# Revit family: VIESSMANN - Vitoradial 300-T
name_source: partatom
category: Wyposażenie mechaniczne
revit_build: Autodesk Revit 2017 (Build: 20160720_1515(x64)
units: mm (PartAtom-declared; Revit-internal decimal feet)

## family parameters
Numer OmniClass = 23.15.30.27.21
Oparty na płaszczyźnie roboczej = Nie
Punkt obliczania pomieszczeń = Nie
Tnij formami wycięć po wczytaniu = Tak
Typ części = Normalny
Tytuł OmniClass = Gas Tanks and Gasholders
Współdzielony = Nie
Wymiar okrągłego złącza = Użyj średnicy
Zawsze pionowo = Tak

## types (6) — shared parameters
Autor = https://www.archispace.pl
Dop. ciśnienie robocze = 400000.0 Pa
Dop. temperatura na zasilaniu (=temperatura progowa) = 110 °C
Numer identyfikacyjny produktu = CE-0035BU104
Opis = Olejowo-gazowy kocioł grzewczy
Opis indeksowy = CE-0035BU104
Parametry spalin - dyspozycyjne ciśnienie tłoczenia na króćcu spalin = 70.0 Pa
Parametry spalin - przepływ masowy przy zastosowaniu lekkiego oleju opałowego = 1.5 x moc spalania w kW
Parametry spalin - przepływ masowy spalin w przypadku gazu ziemnego = 1.5225 x moc spalania w kW
Producent = Viessmann Sp.z.o.o.
Przyłącze spalin = 200 mm  [stored 0.656168 ft]
Sprawność znormalizowana (do eksploatacji na olej opałowy) przy temp. systemu grzewczego 75/60°C = 97 (Hs)/103 (Hi) [%]
Spust = 1 1/4"
URL = https://www.viessmann-projektant.pl
Viessmann Kolor 1 = Viessmann Kolor 1
Viessmann Kolor 2 = Viessmann Kolor 2
Viessmann Kolor 3 = Viessmann Kolor 3
Viessmann Kolor 4 = Viessmann Kolor 4
Wysokość fundamentu = 100 mm  [stored 0.328084 ft]
Występ króćca spalin bez WT = 175 mm  [stored 0.574147 ft]
r+62 = 237 mm  [stored 0.777559 ft]

## per-type parameters (varying)
- VR3 101kW: (t-q)+o=195 mm  [stored 0.639764 ft]; Długość=1300 mm; Długość WT=440 mm  [stored 1.44357 ft]; Długość fundamentu=1000 mm  [stored 3.28084 ft]; Masa całkowita=510.00 kg; Masa korpusu kotła=370.00 kg; Moc nominalna=101000 W; Model=Olejowo-gazowy kocioł kondensacyjny Viessmann Vitoradial 300-T VR3 101kW / Oil-gas condensing boiler Viessmann Vitoradial 300-T VR3 101kW; Odsunięcie króćca zasilania z kotła=165 mm; Odsunięcie powrotu do kotła=620 mm  [stored 2.03412 ft]; Odsunięcie przyłącza zabezpieczającego=320 mm  [stored 1.04987 ft]; Odsunięcie strefy serwisowej z przodu=800 mm  [stored 2.62467 ft]; Opory przepływu=220.0 Pa; Opór przepływu spalin=55.0 Pa; PN 6 DN - powrót do kotła=65 mm  [stored 0.213255 ft]; PN 6 DN - zasilanie z kotła=65 mm  [stored 0.213255 ft]; Parametry spalin - przy obciążeniu częściowym (przy temp. wody na powrocie wyn. 30°C)=30 °C; Parametry spalin - przy znamionowej mocy cieplnej (przy temp. wody na powrocie wyn. 30°C)=35 °C; Parametry spalin - temperatura (przy temp. wody na powrocie wyn. 60°C)=60 °C; Pojemność wodna kotła=185.0 L; Promień a=68 mm; Promień b=85 mm  [stored 0.278871 ft]; Przepływ maksymalny=1.2 L/s; Przyłącze zabezpieczające (zawór bezpieczeństwa)=1 1/4"; Straty energii dyżurnej qB,70=1.5 %; Szerokość=755 mm  [stored 2.47703 ft]; Szerokość fundamentu=760 mm; Szerokość podestu=575 mm  [stored 1.88648 ft]; Wysokośc powrotu do kotła=1370 mm; Wysokośc przyłącza splain bez WT=1460 mm; Wysokość=1085 mm; Wysokość d=440 mm  [stored 1.44357 ft]; Wysokość e=650 mm  [stored 2.13255 ft]; Wysokość konsoli=1315 mm; Wysokość króćća zasilania z kotła=1145 mm; Wysokość spustu=200 mm  [stored 0.656168 ft]; Znamionowe obciążenie cieplne=97000 W; Średnica a=135 mm  [stored 0.442913 ft]
- VR3 129kW: (t-q)+o=190 mm  [stored 0.62336 ft]; Długość=1500 mm; Długość WT=440 mm  [stored 1.44357 ft]; Długość fundamentu=1200 mm; Masa całkowita=545.00 kg; Masa korpusu kotła=405.00 kg; Moc nominalna=129000 W; Model=Olejowo-gazowy kocioł kondensacyjny Viessmann Vitoradial 300-T VR3 129kW / Oil-gas condensing boiler Viessmann Vitoradial 300-T VR3 129kW; Odsunięcie króćca zasilania z kotła=165 mm; Odsunięcie powrotu do kotła=825 mm  [stored 2.70669 ft]; Odsunięcie przyłącza zabezpieczającego=395 mm  [stored 1.29593 ft]; Odsunięcie strefy serwisowej z przodu=950 mm  [stored 3.1168 ft]; Opory przepływu=350.0 Pa; Opór przepływu spalin=80.0 Pa; PN 6 DN - powrót do kotła=65 mm  [stored 0.213255 ft]; PN 6 DN - zasilanie z kotła=65 mm  [stored 0.213255 ft]; Parametry spalin - przy obciążeniu częściowym (przy temp. wody na powrocie wyn. 30°C)=35 °C; Parametry spalin - przy znamionowej mocy cieplnej (przy temp. wody na powrocie wyn. 30°C)=40 °C; Parametry spalin - temperatura (przy temp. wody na powrocie wyn. 60°C)=60 °C; Pojemność wodna kotła=225.0 L; Promień a=120 mm  [stored 0.393701 ft]; Promień b=135 mm  [stored 0.442913 ft]; Przepływ maksymalny=1.5 L/s; Przyłącze zabezpieczające (zawór bezpieczeństwa)=1 1/4"; Straty energii dyżurnej qB,70=1.2 %; Szerokość=755 mm  [stored 2.47703 ft]; Szerokość fundamentu=760 mm; Szerokość podestu=575 mm  [stored 1.88648 ft]; Wysokośc powrotu do kotła=1370 mm; Wysokośc przyłącza splain bez WT=1460 mm; Wysokość=1085 mm; Wysokość d=440 mm  [stored 1.44357 ft]; Wysokość e=650 mm  [stored 2.13255 ft]; Wysokość konsoli=1315 mm; Wysokość króćća zasilania z kotła=1145 mm; Wysokość spustu=200 mm  [stored 0.656168 ft]; Znamionowe obciążenie cieplne=124000 W; Średnica a=240 mm  [stored 0.787402 ft]
- VR3 157kW: (t-q)+o=190 mm  [stored 0.62336 ft]; Długość=1485 mm; Długość WT=440 mm  [stored 1.44357 ft]; Długość fundamentu=1200 mm; Masa całkowita=610.00 kg; Masa korpusu kotła=460.00 kg; Moc nominalna=157000 W; Model=Olejowo-gazowy kocioł kondensacyjny Viessmann Vitoradial 300-T VR3 157kW / Oil-gas condensing boiler Viessmann Vitoradial 300-T VR3 157kW; Odsunięcie króćca zasilania z kotła=150 mm; Odsunięcie powrotu do kotła=810 mm; Odsunięcie przyłącza zabezpieczającego=325 mm  [stored 1.06627 ft]; Odsunięcie strefy serwisowej z przodu=950 mm  [stored 3.1168 ft]; Opory przepływu=500.0 Pa; Opór przepływu spalin=120.0 Pa; PN 6 DN - powrót do kotła=65 mm  [stored 0.213255 ft]; PN 6 DN - zasilanie z kotła=65 mm  [stored 0.213255 ft]; Parametry spalin - przy obciążeniu częściowym (przy temp. wody na powrocie wyn. 30°C)=40 °C; Parametry spalin - przy znamionowej mocy cieplnej (przy temp. wody na powrocie wyn. 30°C)=45 °C; Parametry spalin - temperatura (przy temp. wody na powrocie wyn. 60°C)=65 °C; Pojemność wodna kotła=265.0 L; Promień a=120 mm  [stored 0.393701 ft]; Promień b=135 mm  [stored 0.442913 ft]; Przepływ maksymalny=1.9 L/s; Przyłącze zabezpieczające (zawór bezpieczeństwa)=1 1/4"; Straty energii dyżurnej qB,70=1.1 %; Szerokość=825 mm  [stored 2.70669 ft]; Szerokość fundamentu=830 mm  [stored 2.7231 ft]; Szerokość podestu=650 mm  [stored 2.13255 ft]; Wysokośc powrotu do kotła=1405 mm; Wysokośc przyłącza splain bez WT=1480 mm; Wysokość=1115 mm; Wysokość d=440 mm  [stored 1.44357 ft]; Wysokość e=650 mm  [stored 2.13255 ft]; Wysokość konsoli=1350 mm; Wysokość króćća zasilania z kotła=1180 mm; Wysokość spustu=190 mm  [stored 0.62336 ft]; Znamionowe obciążenie cieplne=151000 W; Średnica a=240 mm  [stored 0.787402 ft]
- VR3 201kW: (t-q)+o=190 mm  [stored 0.62336 ft]; Długość=1680 mm; Długość WT=565 mm  [stored 1.85367 ft]; Długość fundamentu=1400 mm; Masa całkowita=680.00 kg; Masa korpusu kotła=520.00 kg; Moc nominalna=201000 W; Model=Olejowo-gazowy kocioł kondensacyjny Viessmann Vitoradial 300-T VR3 201kW / Oil-gas condensing boiler Viessmann Vitoradial 300-T VR3 201kW; Odsunięcie króćca zasilania z kotła=150 mm; Odsunięcie powrotu do kotła=1010 mm; Odsunięcie przyłącza zabezpieczającego=425 mm  [stored 1.39436 ft]; Odsunięcie strefy serwisowej z przodu=1100 mm; Opory przepływu=800.0 Pa; Opór przepływu spalin=180.0 Pa; PN 6 DN - powrót do kotła=65 mm  [stored 0.213255 ft]; PN 6 DN - zasilanie z kotła=65 mm  [stored 0.213255 ft]; Parametry spalin - przy obciążeniu częściowym (przy temp. wody na powrocie wyn. 30°C)=35 °C; Parametry spalin - przy znamionowej mocy cieplnej (przy temp. wody na powrocie wyn. 30°C)=40 °C; Parametry spalin - temperatura (przy temp. wody na powrocie wyn. 60°C)=60 °C; Pojemność wodna kotła=310.0 L; Promień a=120 mm  [stored 0.393701 ft]; Promień b=135 mm  [stored 0.442913 ft]; Przepływ maksymalny=2.4 L/s; Przyłącze zabezpieczające (zawór bezpieczeństwa)=1 1/4"; Straty energii dyżurnej qB,70=1.0 %; Szerokość=825 mm  [stored 2.70669 ft]; Szerokość fundamentu=830 mm  [stored 2.7231 ft]; Szerokość podestu=650 mm  [stored 2.13255 ft]; Wysokośc powrotu do kotła=1405 mm; Wysokośc przyłącza splain bez WT=1480 mm; Wysokość=1115 mm; Wysokość d=420 mm  [stored 1.37795 ft]; Wysokość e=670 mm  [stored 2.19816 ft]; Wysokość konsoli=1350 mm; Wysokość króćća zasilania z kotła=1180 mm; Wysokość spustu=190 mm  [stored 0.62336 ft]; Znamionowe obciążenie cieplne=194000 W; Średnica a=240 mm  [stored 0.787402 ft]
- VR3 263kW: (t-q)+o=215 mm; Długość=1905 mm; Długość WT=565 mm  [stored 1.85367 ft]; Długość fundamentu=1650 mm; Masa całkowita=870.00 kg; Masa korpusu kotła=700.00 kg; Moc nominalna=263000 W; Model=Olejowo-gazowy kocioł kondensacyjny Viessmann Vitoradial 300-T VR3 263kW / Oil-gas condensing boiler Viessmann Vitoradial 300-T VR3 263kW; Odsunięcie króćca zasilania z kotła=155 mm  [stored 0.50853 ft]; Odsunięcie powrotu do kotła=1180 mm; Odsunięcie przyłącza zabezpieczającego=610 mm  [stored 2.00131 ft]; Odsunięcie strefy serwisowej z przodu=1100 mm; Opory przepływu=1200.0 Pa; Opór przepływu spalin=240.0 Pa; PN 6 DN - powrót do kotła=65 mm  [stored 0.213255 ft]; PN 6 DN - zasilanie z kotła=65 mm  [stored 0.213255 ft]; Parametry spalin - przy obciążeniu częściowym (przy temp. wody na powrocie wyn. 30°C)=35 °C; Parametry spalin - przy znamionowej mocy cieplnej (przy temp. wody na powrocie wyn. 30°C)=40 °C; Parametry spalin - temperatura (przy temp. wody na powrocie wyn. 60°C)=70 °C; Pojemność wodna kotła=490.0 L; Promień a=120 mm  [stored 0.393701 ft]; Promień b=135 mm  [stored 0.442913 ft]; Przepływ maksymalny=3.2 L/s; Przyłącze zabezpieczające (zawór bezpieczeństwa)=1 1/2"; Straty energii dyżurnej qB,70=1.0 %; Szerokość=905 mm  [stored 2.96916 ft]; Szerokość fundamentu=900 mm  [stored 2.95276 ft]; Szerokość podestu=730 mm  [stored 2.39501 ft]; Wysokośc powrotu do kotła=1510 mm; Wysokośc przyłącza splain bez WT=1580 mm; Wysokość=1225 mm; Wysokość d=420 mm  [stored 1.37795 ft]; Wysokość e=670 mm  [stored 2.19816 ft]; Wysokość konsoli=1460 mm; Wysokość króćća zasilania z kotła=1285 mm; Wysokość spustu=135 mm  [stored 0.442913 ft]; Znamionowe obciążenie cieplne=254000 W; Średnica a=240 mm  [stored 0.787402 ft]
- VR3 335kW: (t-q)+o=215 mm; Długość=1905 mm; Długość WT=565 mm  [stored 1.85367 ft]; Długość fundamentu=1650 mm; Masa całkowita=970.00 kg; Masa korpusu kotła=800.00 kg; Moc nominalna=335000 W; Model=Olejowo-gazowy kocioł kondensacyjny Viessmann Vitoradial 300-T VR3 335kW / Oil-gas condensing boiler Viessmann Vitoradial 300-T VR3 335kW; Odsunięcie króćca zasilania z kotła=155 mm  [stored 0.50853 ft]; Odsunięcie powrotu do kotła=1180 mm; Odsunięcie przyłącza zabezpieczającego=610 mm  [stored 2.00131 ft]; Odsunięcie strefy serwisowej z przodu=1300 mm; Opory przepływu=1000.0 Pa; Opór przepływu spalin=275.0 Pa; PN 6 DN - powrót do kotła=80 mm  [stored 0.262467 ft]; PN 6 DN - zasilanie z kotła=80 mm  [stored 0.262467 ft]; Parametry spalin - przy obciążeniu częściowym (przy temp. wody na powrocie wyn. 30°C)=40 °C; Parametry spalin - przy znamionowej mocy cieplnej (przy temp. wody na powrocie wyn. 30°C)=45 °C; Parametry spalin - temperatura (przy temp. wody na powrocie wyn. 60°C)=70 °C; Pojemność wodna kotła=450.0 L; Promień a=120 mm  [stored 0.393701 ft]; Promień b=135 mm  [stored 0.442913 ft]; Przepływ maksymalny=4.0 L/s; Przyłącze zabezpieczające (zawór bezpieczeństwa)=1 1/2"; Straty energii dyżurnej qB,70=0.9 %; Szerokość=905 mm  [stored 2.96916 ft]; Szerokość fundamentu=900 mm  [stored 2.95276 ft]; Szerokość podestu=730 mm  [stored 2.39501 ft]; Wysokośc powrotu do kotła=1510 mm; Wysokośc przyłącza splain bez WT=1580 mm; Wysokość=1225 mm; Wysokość d=420 mm  [stored 1.37795 ft]; Wysokość e=670 mm  [stored 2.19816 ft]; Wysokość konsoli=1460 mm; Wysokość króćća zasilania z kotła=1285 mm; Wysokość spustu=135 mm  [stored 0.442913 ft]; Znamionowe obciążenie cieplne=323000 W; Średnica a=240 mm  [stored 0.787402 ft]

note: [stored X ft] marks values corroborated as IEEE doubles in the binary element streams (Revit-internal decimal feet)
